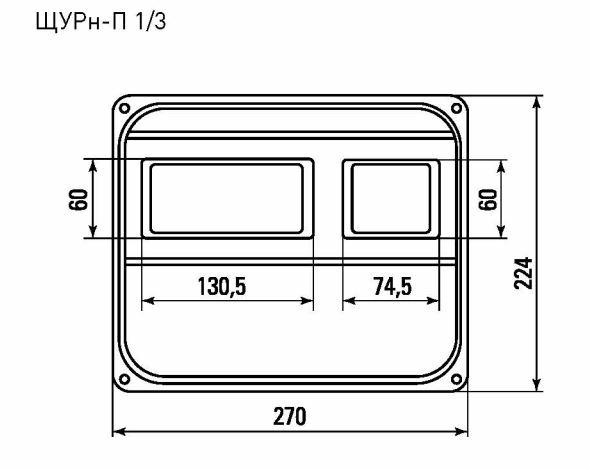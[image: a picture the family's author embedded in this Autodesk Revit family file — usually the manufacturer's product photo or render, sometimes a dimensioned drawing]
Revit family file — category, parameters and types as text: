
# Revit family: EKF_EE_ЩУ_IP54_PROxima
name_source: partatom
category: Электрооборудование
units: mm (PartAtom-declared; Revit-internal decimal feet)

## family parameters
Всегда вертикально = Да
На основе рабочей плоскости = Нет
Общий = Нет
При загрузке вырезать с полостями = Нет
Размер круглого соединителя = Использовать диаметр
Тип детали = Силовой щит
Точка расчета площади = Да

## types (9) — shared parameters
ADSK_Единица измерения = компл.
ADSK_Завод-изготовитель = EKF
ADSK_Классификация нагрузок = Прочее
ADSK_Количество = 1
ADSK_Количество фаз = 3
ADSK_Коэффициент мощности = 1
ADSK_Материал = RAL 7035_Сталь
ADSK_Напряжение = 400 В
ADSK_Номинальная мощность = 0 Вт
ADSK_Полная мощность = 0 В·А
ADSK_Ток = 125 А
Изготовитель = EKF
Серия номенклатуры = PROxima
Степень защиты IP = IP54
ТВ = EKF
Тип установки = Навесной
zero-valued in all types: Количество DIN-реек, Максимальное количество модулей

## per-type parameters (varying)
| type | ADSK_Код изделия | ADSK_Марка | ADSK_Масса | ADSK_Наименование | ADSK_Обозначение | ADSK_Размер_Высота | ADSK_Размер_Глубина | ADSK_Размер_Ширина | Количество модулей на DIN-рейке | Описание | Тип |
| ЩУРн-3/12 два отсека (БУР) (540х300х160) IP54 EKF PROxima | mb54-3i | ЩУРн-3/12 два отсека (БУР) IP54 | 6.7 | Щит учетно-распред. навесной ЩУРн-3/12 два отсека (БУР) (540х300х160) IP54 EKF PROxima | ЩУРн-3/12 два отсека (БУР) IP54 | 540 мм | 160 мм | 300 мм | 12 | Щит учетно-распред. навесной ЩУРн-3/12 два отсека (БУР) (540х300х160) IP54 EKF PROxima | 46 мм |
| ЩУ-1/1-0 (310х300х150) IP54 EKF PROxima | mb54-1 | ЩУ-1/1-0 IP54 | 4.78 | Щит учетный ЩУ-1/1-0 (310х300х150) IP54 EKF PROxima | ЩУ-1/1-0 IP54 | 310 мм | 150 мм | 300 мм | 3 | Щит учетный ЩУ-1/1-0 (310х300х150) IP54 EKF PROxima | 47 мм |
| ЩУ-1/1-0 (395x310x165) (ЩУРН-1/12) IP54 EKF PROxima | mb54-1m | ЩУ-1/1-0 (ЩУРН-1/12) IP54 | 4.5 | Щит учетный ЩУ-1/1-0 (395x310x165) (ЩУРН-1/12) IP54 EKF PROxima | ЩУ-1/1-0 (ЩУРН-1/12) IP54 | 395 мм | 165 мм | 310 мм | 12 | Щит учетный ЩУ-1/1-0 (395x310x165) (ЩУРН-1/12) IP54 EKF PROxima | 48 мм |
| ЩУ-1/1-1 двухдверный (310х300х160) IP54 EKF PROxima | mb54-1-2 | ЩУ-1/1-1 двухдверный  IP54 | 5.23 | Щит учетный ЩУ-1/1-1 двухдверный (310х300х160) IP54 EKF PROxima | ЩУ-1/1-1 двухдверный  IP54 | 310 мм | 160 мм | 300 мм | 6 | Щит учетный ЩУ-1/1-1 двухдверный (310х300х160) IP54 EKF PROxima | 49 мм |
| ЩУ-1/2-0 (310х420х150) IP54 EKF PROxima | mb54-2 | ЩУ-1/2-0 IP54 | 4.69 | Щит учетный ЩУ-1/2-0 (310х420х150) IP54 EKF PROxima | ЩУ-1/2-0 IP54 | 310 мм | 150 мм | 420 мм | 3 | Щит учетный ЩУ-1/2-0 (310х420х150) IP54 EKF PROxima | 50 мм |
| ЩУ-3/1-0 (395x310x150) IP54 EKF PROxima | mb54-3m | ЩУ-3/1-0 IP54 | 4.55 | Щит учетный ЩУ-3/1-0 (395x310x150) IP54 EKF PROxima | ЩУ-3/1-0 IP54 | 395 мм | 150 мм | 310 мм | 3 | Щит учетный ЩУ-3/1-0 (395x310x150) IP54 EKF PROxima | 51 мм |
| ЩУ-3/1-0 (ЩУРН-3/12) (540x310x165) 12 модулей IP54 EKF PROxima | mb54-3 | ЩУ-3/1-0 (ЩУРН-3/12) 12 модулей IP54 | 5.3 | Щит учетный ЩУ-3/1-0 (ЩУРН-3/12) (540x310x165) 12 модулей IP54 EKF PROxima | ЩУ-3/1-0 (ЩУРН-3/12) 12 модулей IP54 | 540 мм | 165 мм | 310 мм | 12 | Щит учетный ЩУ-3/1-0 (ЩУРН-3/12) (540x310x165) 12 модулей IP54 EKF PROxima | 52 мм |
| ЩУ-3/1-1 двухдверный (445x400x150) 12 модулей IP54 EKF PROxima | mb54-3-2 | ЩУ-3/1-1 двухдверный 12 модулей IP54 | 7.55 | Щит учетный ЩУ-3/1-1 двухдверный (445x400x150) 12 модулей IP54 EKF PROxima | ЩУ-3/1-1 двухдверный 12 модулей IP54 | 445 мм | 150 мм | 400 мм | 12 | Щит учетный ЩУ-3/1-1 двухдверный (445x400x150) 12 модулей IP54 EKF PROxima | 53 мм |
| ЩУ-1/1-0 (250х300х100) IP54 EKF PROxima | mb54-1E | На дин-рейку ЩУ-1/1-0 IP54 | 2.2 | Щит учетный для счетчика на дин-рейку ЩУ-1/1-0 (250х300х100) IP54 EKF PROxima | На дин-рейку ЩУ-1/1-0 IP54 | 250 мм | 100 мм | 300 мм | 12 | Щит учетный для счетчика на дин-рейку ЩУ-1/1-0 (250х300х100) IP54 EKF PROxima | 54 мм |
